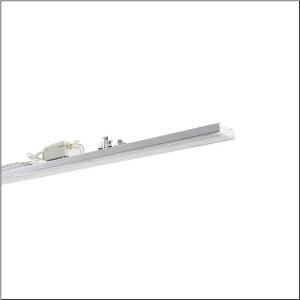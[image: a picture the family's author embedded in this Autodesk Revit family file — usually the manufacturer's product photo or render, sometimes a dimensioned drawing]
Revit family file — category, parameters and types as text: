
# Revit family: licross_r__21_recessed_mo_52tl1ecn48xg_a19d
name_source: partatom
category: Lighting Fixtures
units: mm (PartAtom-declared; Revit-internal decimal feet)

## family parameters
Cut with Voids When Loaded = No
Host = Face
Light Source = No
Part Type = Normal
Room Calculation Point = No
Round Connector Dimension = Use Diameter
Shared = No

## types (1)
- --- (1 x LED, 8020 lm, 44.4 W, 4000K)
    Apparent Load = 44 VA
    CIE Flux Codes = 85 95 99 100 100
    Color Rendering = 80
    Color Temperature = 4000K
    Default Elevation = 1800 mm
    Description = Licross® 21 Recessed MO, luminaire insert, of sheet steel, galvanised, coil coated, white, length: 1.500mm, width: 66mm, height: 67mm, LED rated luminous flux: 8.030lm, light colour: 840, control gear: ON/OFF Multilumen, CLOi, control gear: ECG Multilumen, with plug, 3-pole, with phase selection, mains connection: 220..240V, AC, 50/60Hz, start of lifetime: 44W, end of service life: 53W, halogen-free wiring, primary light control with lens, of plastic, primary optical cover: cover, of PMMA, light emission: direct distribution, primary light characteristic: symmetric, protection rating (complete): IP40, insulation class (complete): insulation class I (protective earthing), certification: CE, ENEC, VDE, UKCA, protection symbol: D if used in an environment without relevant dust loads with corresponding accessories, impact resistance: IK06, permissible ambient temperature for indoor applications: -35..+45°C, corresponds to IFS (International Featured Standards) requirements for safety and quality in the food industry, reducing of maximum allowable ambient temperature of 5°C with ceiling mounting, LABS conformity tested according to VDMA 24364:2018-05, packaging unit: 1 piece
    Height = 58 mm
    Lamp = 1 x LED
    Lamp Light Flux = 8020 lm
    Lamp Power = 44.4 W
    Lamp count = 1
    Length = 1500 mm
    Luminous efficacy = 181 lm/W
    Manufacturer = Siteco
    ModVariant = No
    Model = 52TL1ECN48XG
    Mounting Place = Ceiling
    Mounting Type = Pendant
    Number of Poles = 1
    OnlyDefault = Yes
    Power Factor = 1
    Product Name = Licross® 21 Recessed MO
    Product group = luminaire insert
    ProductGroupID = 901
    Protection Class = Protection class I
    Protection Degree = IP 40
    RLX_Detail_Level = 1
    RLX_Emergency_Light_Flux = 0 lm
    RLX_Emergency_Type = 0
    RLX_Emergency_Type_DB = No
    RlxData = <blob elided: 22357 chars, md5=96e002a1>
    Socket = socket
    Standby Power = 0 W
    System Light Flux = 8020 lm
    System Power = 44 W
    Type Comments = factory setting: luminous flux: 100 % | (A | C | E) | 103 mA
    Type Image = l_1296930.jpg
    URL = http://relux.com
    VarID = @adj_040081
    Voltage = 0 V
    Weight = 0.00 kg
    Width = 66 mm

## geometry (parser evidence)
native form markers: Blend x4, Sweep x12
no freeform markers — native parametric forms only
